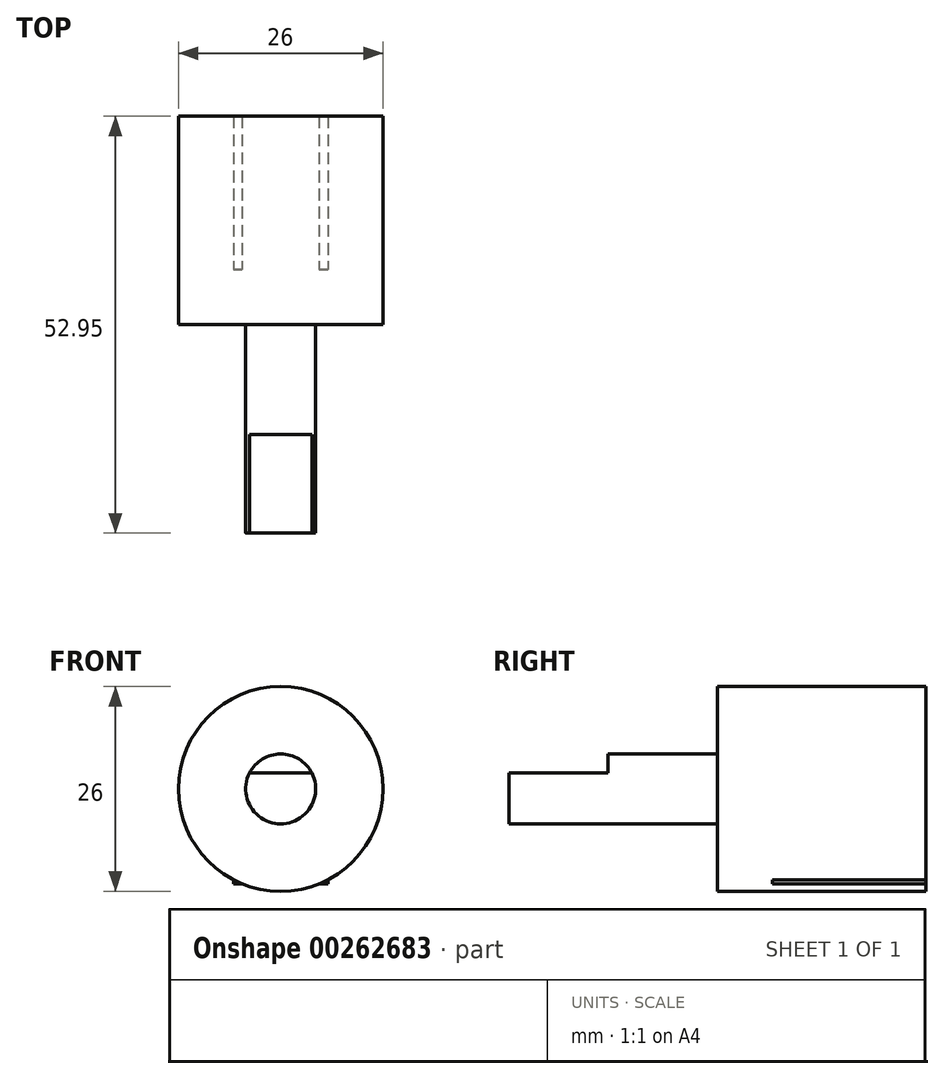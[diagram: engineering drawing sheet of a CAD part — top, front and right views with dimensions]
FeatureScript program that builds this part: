
annotation { "Feature Type Name" : "Feature", "Feature Type Description" : "" }
export const myFeature = defineFeature(function(context is Context, id is Id, definition is map)
    precondition{}
    {
        {
            var Q0;
            Q0=qCreatedBy(makeId("Front.planeOp"),FACE);
            var sketch = newSketch(context, id + "F0", { "sketchPlane" : qUnion([Q0])});
            skLineSegment(sketch, "E0.bottom", {"start": v(6, -2.75) * mm, "end": v(-6, -2.75) * mm});
            skLineSegment(sketch, "E0.top", {"start": v(6, 2.75) * mm, "end": v(-6, 2.75) * mm});
            skLineSegment(sketch, "E0.left", {"start": v(6, -2.75) * mm, "end": v(6, 2.75) * mm});
            skLineSegment(sketch, "E0.right", {"start": v(-6, -2.75) * mm, "end": v(-6, 2.75) * mm});
            skPoint(sketch, "E0.middle", {"position": v(0, 0) * mm});
            skSolve(sketch);
        }
        {
            var Q0;
            Q0=makeQuery(id+"F0.imprint","IMPRINT",FACE,{"disambiguationData":[TD([[makeQuery(id+"F0.imprint","IMPRINT",EDGE,{"derivedFrom":sQuery(id+"F0.wireOp",EDGE,"E0.bottom")}),-1.0]])]});
            extrude(context, id + "F1", {"entities" : qUnion([Q0]), "oppositeDirection" : true, "depth" : 19.5 * mm});
        }
        {
            var Q0;
            Q0=makeQuery(id+"F1.opExtrude","CAP_FACE",FACE,{"disambiguationData":[OSD([sQuery(id+"F0.wireOp",EDGE,"E0.bottom"),sQuery(id+"F0.wireOp",EDGE,"E0.top"),sQuery(id+"F0.wireOp",EDGE,"E0.left"),sQuery(id+"F0.wireOp",EDGE,"E0.right")])],"isStart":true});
            cPlane(context, id + "F2", {"entities" : qUnion([Q0]), "cplaneType" : CPlaneType.OFFSET, "offset" : 6.95 * mm, "width" : 150 * mm, "height" : 150 * mm});
        }
        {
            var Q0;
            Q0=qCreatedBy(id+"F2.planeOp",FACE);
            var sketch = newSketch(context, id + "F3", { "sketchPlane" : qUnion([Q0])});
            skCircle(sketch, "E1", {"center": v(0, 9.3) * mm, "radius": 13 * mm});
            skSolve(sketch);
        }
        {
            var Q0;
            Q0=makeQuery(id+"F3.imprint","IMPRINT",FACE,{"disambiguationData":[TD([[makeQuery(id+"F3.imprint","IMPRINT",EDGE,{"derivedFrom":sQuery(id+"F3.wireOp",EDGE,"E1")}),1.0]])]});
            var Q1;
            Q1=makeQuery(id+"F1.opExtrude","CAP_FACE",FACE,{"disambiguationData":[OSD([sQuery(id+"F0.wireOp",EDGE,"E0.bottom"),sQuery(id+"F0.wireOp",EDGE,"E0.top"),sQuery(id+"F0.wireOp",EDGE,"E0.left"),sQuery(id+"F0.wireOp",EDGE,"E0.right")])],"isStart":false});
            extrude(context, id + "F4", {"entities" : qUnion([Q0]), "operationType" : NewBodyOperationType.ADD, "endBound" : BoundingType.UP_TO_SURFACE, "oppositeDirection" : true, "endBoundEntityFace" : qUnion([Q1]), "depth" : 25 * mm});
        }
        {
            var Q0;
            Q0=qCreatedBy(id+"F2.planeOp",FACE);
            var sketch = newSketch(context, id + "F5", { "sketchPlane" : qUnion([Q0])});
            skCircle(sketch, "E2.0.0", {"center": v(0, 9.3) * mm, "radius": 13 * mm});
            skCircle(sketch, "E3", {"center": v(0, 9.3) * mm, "radius": 4.45 * mm});
            skSolve(sketch);
        }
        {
            var Q0;
            Q0=makeQuery(id+"F5.imprint","IMPRINT",FACE,{"disambiguationData":[TD([[makeQuery(id+"F5.imprint","IMPRINT",EDGE,{"derivedFrom":sQuery(id+"F5.wireOp",EDGE,"E3")}),1.0]])]});
            var Q1;
            Q1=sQuery(id+"F5.wireOp",EDGE,"E3");
            extrude(context, id + "F6", {"entities" : qUnion([Q0]), "operationType" : NewBodyOperationType.ADD, "surfaceEntities" : qUnion([Q1]), "depth" : 13.95 * mm});
        }
        {
            var Q0;
            Q0=makeQuery(id+"F6.opExtrude","CAP_FACE",FACE,{"disambiguationData":[OSD([sQuery(id+"F5.wireOp",EDGE,"E3")])],"isStart":false});
            cPlane(context, id + "F7", {"entities" : qUnion([Q0]), "cplaneType" : CPlaneType.OFFSET, "offset" : 0 * mm, "width" : 150 * mm, "height" : 150 * mm});
        }
        {
            var Q0;
            Q0=qCreatedBy(id+"F7.planeOp",FACE);
            var sketch = newSketch(context, id + "F8", { "sketchPlane" : qUnion([Q0])});
            skCircle(sketch, "E4.0.0", {"center": v(0, 9.3) * mm, "radius": 4.45 * mm});
            skLineSegment(sketch, "E5", {"start": v(0, 4.86) * mm, "end": v(0, 11.34) * mm});
            skLineSegment(sketch, "E6", {"start": v(0, 11.34) * mm, "end": v(3.95, 11.34) * mm});
            skLineSegment(sketch, "E7", {"start": v(0, 11.34) * mm, "end": v(-3.95, 11.34) * mm});
            skSolve(sketch);
        }
        {
            var Q0;
            {var subQ0=sQuery(id+"F8.wireOp",EDGE,"E5");Q0=makeQuery(id+"F8.imprint","IMPRINT",FACE,{"disambiguationData":[TD([[makeQuery(id+"F8.imprint","IMPRINT",EDGE,{"derivedFrom":subQ0}),-1.0]])]});}
            var Q1;
            {var subQ0=sQuery(id+"F8.wireOp",EDGE,"E5");Q1=makeQuery(id+"F8.imprint","IMPRINT",FACE,{"disambiguationData":[TD([[makeQuery(id+"F8.imprint","IMPRINT",EDGE,{"derivedFrom":subQ0}),1.0]])]});}
            extrude(context, id + "F9", {"entities" : qUnion([Q0, Q1]), "operationType" : NewBodyOperationType.ADD, "depth" : 12.55 * mm});
        }
    });
